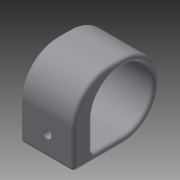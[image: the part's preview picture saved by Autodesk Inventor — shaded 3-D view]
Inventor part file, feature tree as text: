
AUTODESK INVENTOR PART (.ipt)
format: ipt  version: 2014 (Build 180170000, 170)  size: 221,696 bytes
history: native  units: mm
features: fillet x12, sketch x4, extrude x3, plane x2, hole x1, chamfer x1
ambient origin geometry x8: Origin, YZ Plane, XZ Plane, XY Plane, X Axis, Y Axis, Z Axis, Center Point
bodies: Volumenkörper1 (feature_tree)
feature tree (23):
  extrude  "Extrusion1"  Depth=36.0mm
  extrude  "Extrusion2"  Depth=3.0mm
  fillet  "Rundung1"  Radius=30.0mm
  fillet  "Rundung2"  Radius=3.0mm
  fillet  "Rundung3"  Radius=3.0mm
  plane  "Arbeitsebene1"
  plane  "Arbeitsebene2"
  extrude  "Extrusion3"  Depth=15.0mm
  fillet  "Rundung4"  Radius=15.0mm
  hole  "Bohrung1"  [1 undecoded]
  fillet  "Rundung10"  [1 undecoded]
  fillet  "Rundung11"  Radius=20.0mm
  fillet  "Rundung12"  Radius=17.0mm
  fillet  "Rundung13"  Radius=3.0mm
  chamfer  "Fase1"  Distance=26.0mm
  fillet  "Rundung6"  Radius=9.0mm
  fillet  "Rundung7"  Radius=13.0mm
  fillet  "Rundung8"  Radius=10.0mm
  fillet  "Rundung9"  Radius=1.5mm
  sketch  "Skizze1"  dims[d0=42.0mm d1=36.0mm]
  sketch  "Skizze2"  dims[d2=26.0mm d3=0.0mm d4=30.0mm d5=30.0mm d6=3.0mm d7=3.0mm]
  sketch  "Skizze3"  dims[d8=26.0mm d9=0.0mm d10=15.0mm d11=15.0mm]
  sketch  "Skizze4"  dims[d12=18.0mm d13=-3.0mm d14=-6.2mm d15=20.0mm d16=17.0mm d17=3.0mm d18=26.0mm d19=0.0mm d20=9.0mm d21=4.2mm d22=6.0mm d23=7.5mm d24=2.0mm d25=90.0deg d26=8.0mm d27=20.594885mm d29=13.0mm d31=10.0mm d32=1.5mm d33=1.5mm d34=1.5mm d35=1.5mm d36=15.0mm d37=18.0mm d38=1.5mm d39=1.5mm d40=0.5mm d41=2.0mm d42=45.0deg]
note: 2 required parameter values undecoded (feature->parameter linkage not recoverable at this tier; creation-order binding heuristic only, values carry confidence <= 0.55)
